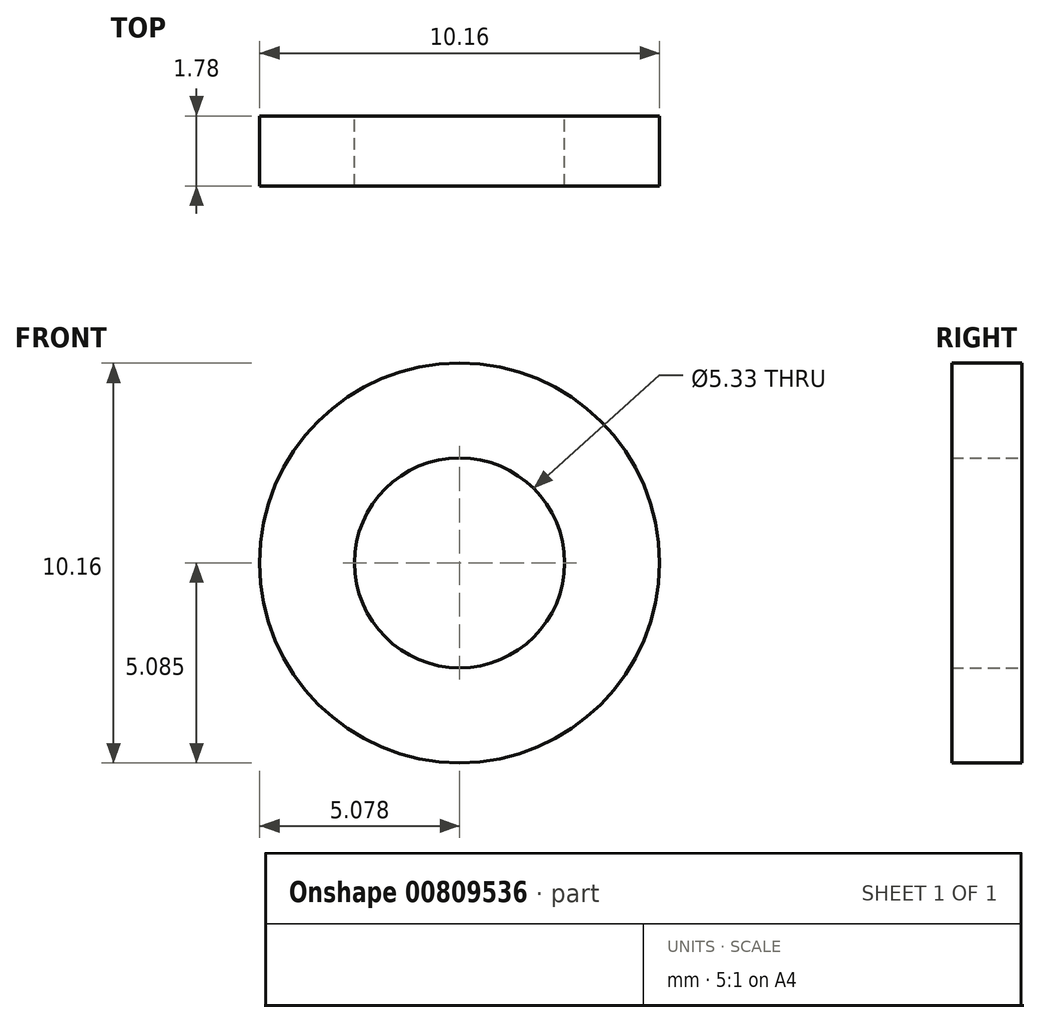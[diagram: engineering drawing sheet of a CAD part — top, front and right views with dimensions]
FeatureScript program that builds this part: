
annotation { "Feature Type Name" : "Feature", "Feature Type Description" : "" }
export const myFeature = defineFeature(function(context is Context, id is Id, definition is map)
    precondition{}
    {
        {
            var Q0;
            Q0=qCreatedBy(makeId("Front.planeOp"),FACE);
            var sketch = newSketch(context, id + "F0", { "sketchPlane" : qUnion([Q0])});
            skCircle(sketch, "E0", {"center": v(-12.16, 4.86) * mm, "radius": 2.67 * mm});
            skCircle(sketch, "E1", {"center": v(-12.16, 4.86) * mm, "radius": 5.08 * mm});
            skSolve(sketch);
        }
        {
            var Q0;
            Q0=makeQuery(id+"F0.imprint","IMPRINT",FACE,{"disambiguationData":[TD([[makeQuery(id+"F0.imprint","IMPRINT",EDGE,{"derivedFrom":sQuery(id+"F0.wireOp",EDGE,"E0")}),-1.0]])]});
            extrude(context, id + "F1", {"entities" : qUnion([Q0]), "depth" : 1.78 * mm, "offsetDistance" : 25.4 * mm});
        }
    });
